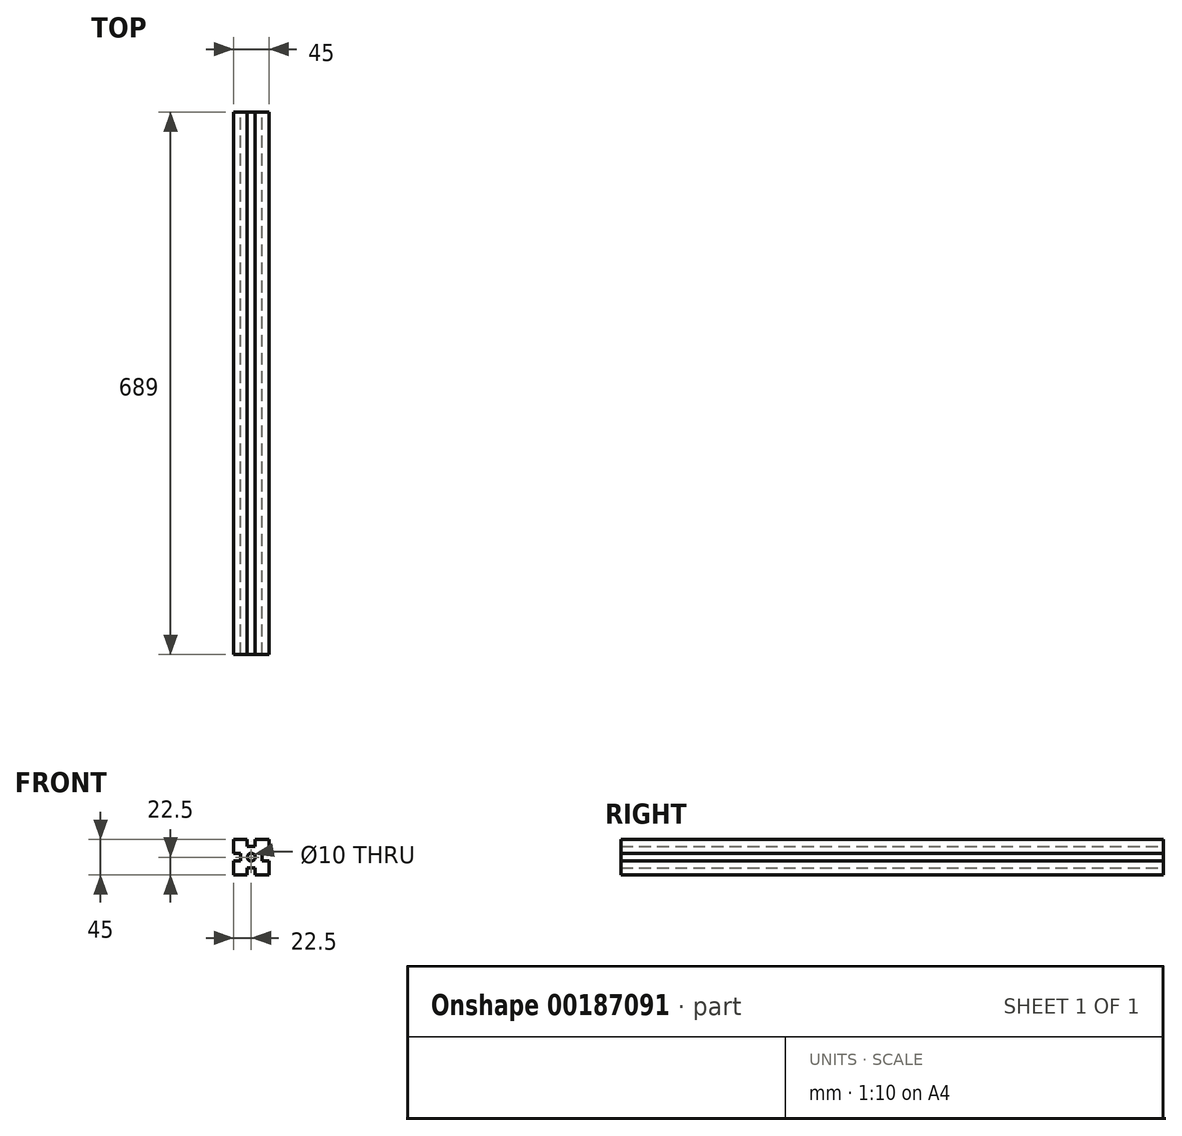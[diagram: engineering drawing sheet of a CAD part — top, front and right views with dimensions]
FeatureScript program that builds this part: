
annotation { "Feature Type Name" : "Feature", "Feature Type Description" : "" }
export const myFeature = defineFeature(function(context is Context, id is Id, definition is map)
    precondition{}
    {
        {
            var Q0;
            Q0=qCreatedBy(makeId("Front.planeOp"),FACE);
            var sketch = newSketch(context, id + "F0", { "sketchPlane" : qUnion([Q0])});
            skLineSegment(sketch, "E0.bottom", {"start": v(22.5, -22.5) * mm, "end": v(5, -22.5) * mm});
            skLineSegment(sketch, "E0.top", {"start": v(22.5, 22.5) * mm, "end": v(5, 22.5) * mm});
            skLineSegment(sketch, "E0.left", {"start": v(22.5, -22.5) * mm, "end": v(22.5, -5) * mm});
            skLineSegment(sketch, "E0.right", {"start": v(-22.5, -22.5) * mm, "end": v(-22.5, -5) * mm});
            skPoint(sketch, "E0.middle", {"position": v(0, 0) * mm});
            skCircle(sketch, "E1", {"center": v(0, 0) * mm, "radius": 5 * mm});
            skLineSegment(sketch, "E2", {"start": v(-22.5, 5) * mm, "end": v(-13.75, 5) * mm});
            skLineSegment(sketch, "E3", {"start": v(-22.5, -5) * mm, "end": v(-13.75, -5) * mm});
            skLineSegment(sketch, "E4", {"start": v(-5, 22.5) * mm, "end": v(-5, 13.75) * mm});
            skLineSegment(sketch, "E5", {"start": v(5, 22.5) * mm, "end": v(5, 13.75) * mm});
            skLineSegment(sketch, "E6", {"start": v(-13.75, 5) * mm, "end": v(-13.75, -5) * mm});
            skLineSegment(sketch, "E7", {"start": v(13.75, 5) * mm, "end": v(13.75, -5) * mm});
            skLineSegment(sketch, "E8", {"start": v(-5, 13.75) * mm, "end": v(5, 13.75) * mm});
            skLineSegment(sketch, "E9.trimOffspring", {"start": v(-22.5, 5) * mm, "end": v(-22.5, 22.5) * mm});
            skLineSegment(sketch, "E10.trimOffspring", {"start": v(-5, 22.5) * mm, "end": v(-22.5, 22.5) * mm});
            skLineSegment(sketch, "E11.trimOffspring", {"start": v(22.5, 5) * mm, "end": v(22.5, 22.5) * mm});
            skLineSegment(sketch, "E12.trimOffspring", {"start": v(-5, -22.5) * mm, "end": v(-22.5, -22.5) * mm});
            skPoint(sketch, "E13.orphan", {"position": v(-13.75, 22.5) * mm});
            skLineSegment(sketch, "E14.trimOffspring", {"start": v(-5, -13.75) * mm, "end": v(-5, -22.5) * mm});
            skPoint(sketch, "E15.trimOffspring.end.orphan", {"position": v(22.5, 13.75) * mm});
            skPoint(sketch, "E16.orphan", {"position": v(13.75, 22.5) * mm});
            skLineSegment(sketch, "E17.trimOffspring", {"start": v(13.75, -5) * mm, "end": v(22.5, -5) * mm});
            skLineSegment(sketch, "E18.trimOffspring", {"start": v(5, -13.75) * mm, "end": v(5, -22.5) * mm});
            skLineSegment(sketch, "E19.trimOffspring", {"start": v(13.75, 5) * mm, "end": v(22.5, 5) * mm});
            skLineSegment(sketch, "E20.trimOffspring", {"start": v(-5, -13.75) * mm, "end": v(5, -13.75) * mm});
            skPoint(sketch, "E21.trimOffspring.end.orphan", {"position": v(22.5, -13.75) * mm});
            skSolve(sketch);
        }
        {
            var Q0;
            Q0=makeQuery(id+"F0.imprint","IMPRINT",FACE,{"disambiguationData":[TD([[makeQuery(id+"F0.imprint","IMPRINT",EDGE,{"derivedFrom":sQuery(id+"F0.wireOp",EDGE,"E0.bottom")}),-1.0]])]});
            extrude(context, id + "F1", {"entities" : qUnion([Q0]), "depth" : 689 * mm});
        }
    });
